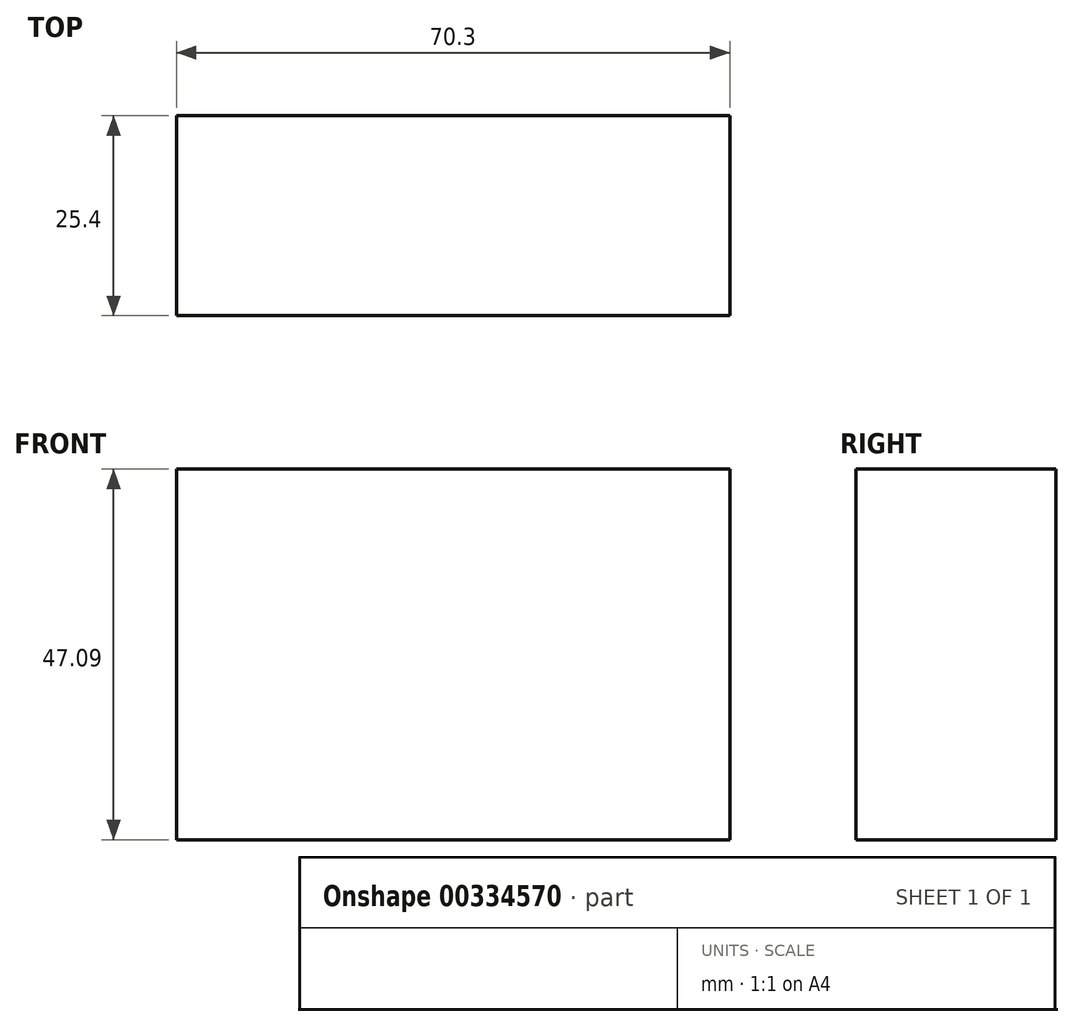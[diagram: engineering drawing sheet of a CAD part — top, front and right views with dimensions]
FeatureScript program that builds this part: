
annotation { "Feature Type Name" : "Feature", "Feature Type Description" : "" }
export const myFeature = defineFeature(function(context is Context, id is Id, definition is map)
    precondition{}
    {
        {
            var Q0;
            Q0=qCreatedBy(makeId("Front.planeOp"),FACE);
            var sketch = newSketch(context, id + "F0", { "sketchPlane" : qUnion([Q0])});
            skLineSegment(sketch, "E0.bottom", {"start": v(14.1, 0) * mm, "end": v(-56.2, 0) * mm});
            skLineSegment(sketch, "E0.top", {"start": v(14.1, 47.09) * mm, "end": v(-56.2, 47.09) * mm});
            skLineSegment(sketch, "E0.left", {"start": v(14.1, 0) * mm, "end": v(14.1, 47.09) * mm});
            skLineSegment(sketch, "E0.right", {"start": v(-56.2, 0) * mm, "end": v(-56.2, 47.09) * mm});
            skSolve(sketch);
        }
        {
            var Q0;
            Q0=makeQuery(id+"F0.imprint","IMPRINT",FACE,{"disambiguationData":[TD([[makeQuery(id+"F0.imprint","IMPRINT",EDGE,{"derivedFrom":sQuery(id+"F0.wireOp",EDGE,"E0.bottom")}),-1.0]])]});
            extrude(context, id + "F1", {"entities" : qUnion([Q0]), "depth" : 25.4 * mm});
        }
    });
